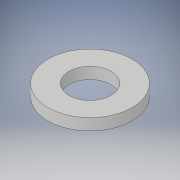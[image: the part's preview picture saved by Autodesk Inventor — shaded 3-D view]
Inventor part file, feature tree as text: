
AUTODESK INVENTOR PART (.ipt)
format: ipt  version: 2017 (Build 210142000, 142)  size: 97,792 bytes
history: native  units: in
note: dims shown in document units (in); Inventor stores cm internally (conversion verified against a paired STEP export)
features: extrude x1, hole x1, sketch x1
ambient origin geometry x8: Origin, YZ Plane, XZ Plane, XY Plane, X Axis, Y Axis, Z Axis, Center Point
bodies: Solid1 (feature_tree)
feature tree (3):
  extrude  "Extrusion1"  Depth=0.12in TaperAngle=0.0deg
  hole  "Hole1"  [1 undecoded]
  sketch  "Sketch1"  dims[d0=0.875in d1=0.12in d2=0.0in d3=1.0in d4=1.0in d5=0.4375in d6=0.75in d7=0.375in d8=0.25in d9=0.5635in d10=0.4375in d11=0.8108in]
note: 1 required parameter value undecoded (feature->parameter linkage not recoverable at this tier; creation-order binding heuristic only, values carry confidence <= 0.55)
